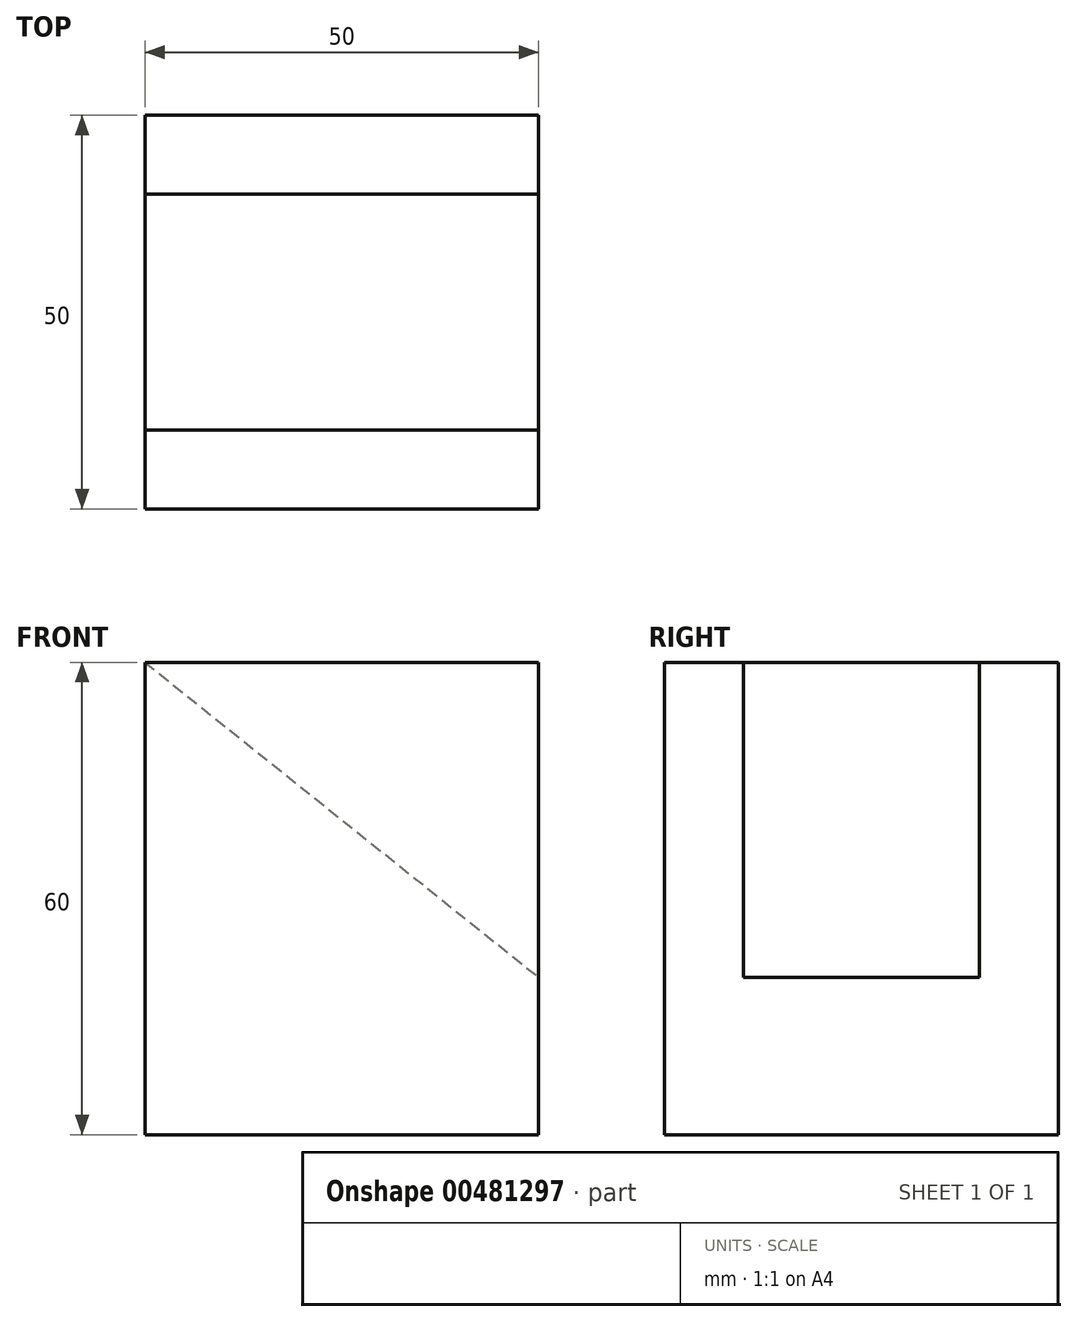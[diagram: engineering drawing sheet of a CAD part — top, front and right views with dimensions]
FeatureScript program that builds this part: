
annotation { "Feature Type Name" : "Feature", "Feature Type Description" : "" }
export const myFeature = defineFeature(function(context is Context, id is Id, definition is map)
    precondition{}
    {
        {
            var Q0;
            Q0=qCreatedBy(makeId("Right.planeOp"),FACE);
            var sketch = newSketch(context, id + "F0", { "sketchPlane" : qUnion([Q0])});
            skLineSegment(sketch, "E0", {"start": v(0, 0) * mm, "end": v(0, 60) * mm});
            skLineSegment(sketch, "E1", {"start": v(0, 60) * mm, "end": v(10, 60) * mm});
            skLineSegment(sketch, "E2", {"start": v(10, 60) * mm, "end": v(10, 20) * mm});
            skLineSegment(sketch, "E3", {"start": v(10, 20) * mm, "end": v(40, 20) * mm});
            skLineSegment(sketch, "E4", {"start": v(40, 20) * mm, "end": v(40, 60) * mm});
            skLineSegment(sketch, "E5", {"start": v(40, 60) * mm, "end": v(50, 60) * mm});
            skLineSegment(sketch, "E6", {"start": v(50, 60) * mm, "end": v(50, 0) * mm});
            skLineSegment(sketch, "E7", {"start": v(50, 0) * mm, "end": v(0, 0) * mm});
            skSolve(sketch);
        }
        {
            var Q0;
            Q0 = qSketchRegion(id + "F0", true);
            extrude(context, id + "F1", {"entities" : qUnion([Q0]), "depth" : 50 * mm});
        }
        {
            var Q0;
            Q0=qCreatedBy(makeId("Front.planeOp"),FACE);
            var sketch = newSketch(context, id + "F2", { "sketchPlane" : qUnion([Q0])});
            skLineSegment(sketch, "E8", {"start": v(0, 60) * mm, "end": v(50, 20) * mm});
            skLineSegment(sketch, "E9", {"start": v(0, 60) * mm, "end": v(0, 20) * mm});
            skLineSegment(sketch, "E10", {"start": v(0, 20) * mm, "end": v(50, 20) * mm});
            skSolve(sketch);
        }
        {
            var Q0;
            Q0 = qSketchRegion(id + "F2", true);
            extrude(context, id + "F3", {"entities" : qUnion([Q0]), "operationType" : NewBodyOperationType.ADD, "oppositeDirection" : true, "depth" : 40 * mm});
        }
    });
